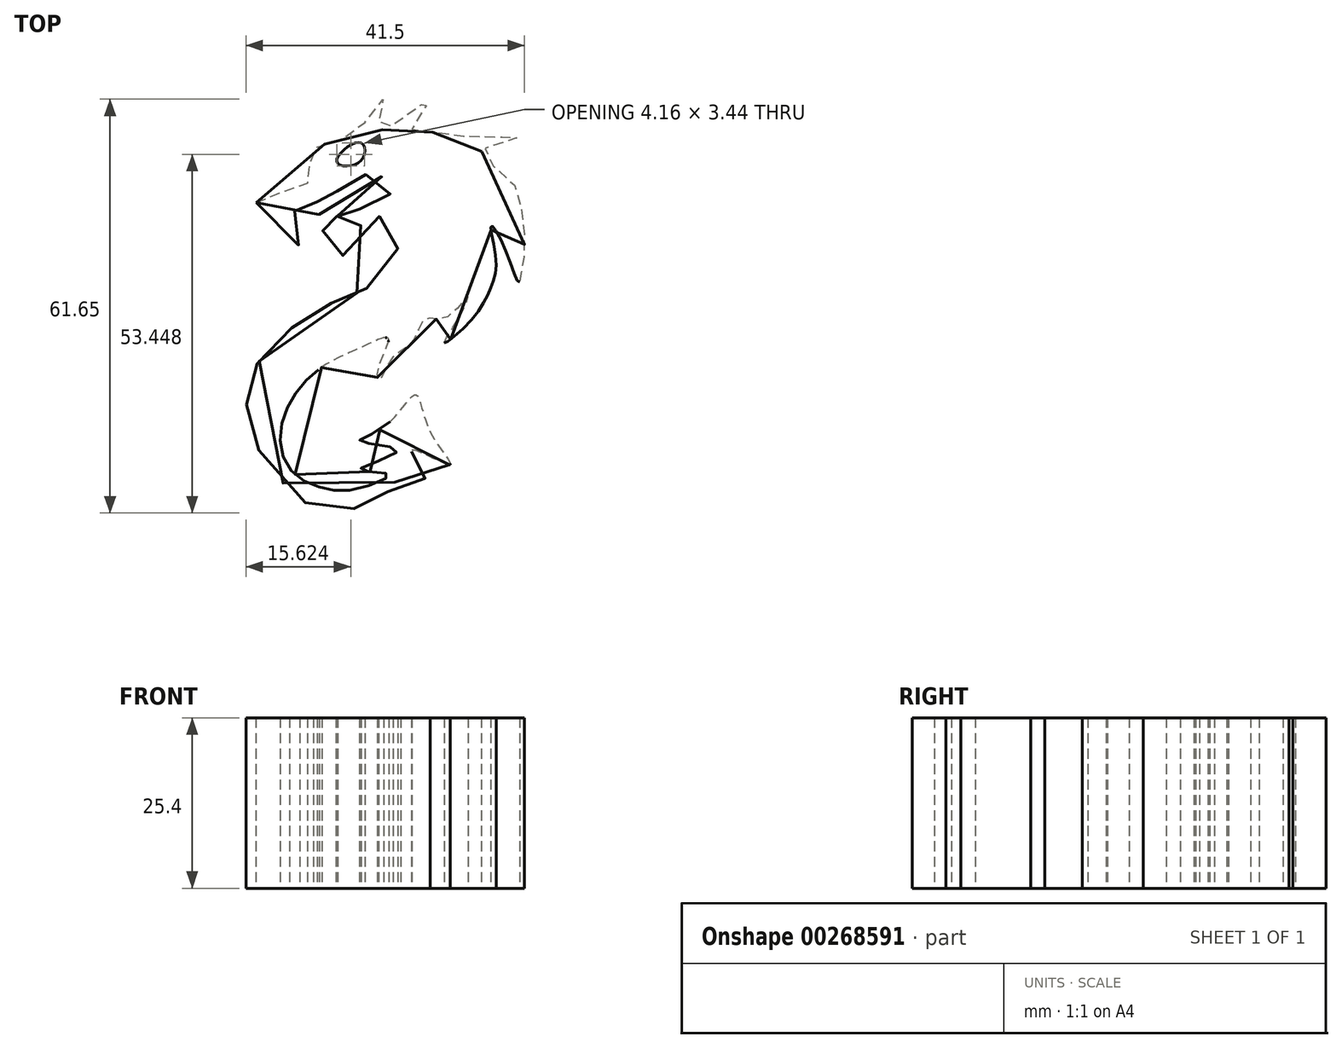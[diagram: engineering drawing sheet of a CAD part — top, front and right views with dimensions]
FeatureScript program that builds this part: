
annotation { "Feature Type Name" : "Feature", "Feature Type Description" : "" }
export const myFeature = defineFeature(function(context is Context, id is Id, definition is map)
    precondition{}
    {
        {
            var Q0;
            Q0=qCreatedBy(makeId("Top.planeOp"),FACE);
            var sketch = newSketch(context, id + "F0", { "sketchPlane" : qUnion([Q0])});
            skFitSpline(sketch, "E0", {"points": [v(-15.49, 17.26) * mm, v(-11.85, 18.65) * mm, v(-6.97, 21.44) * mm, v(-7.81, 24.23) * mm, v(-4.18, 26.32) * mm, v(0, 28.41) * mm, v(3.49, 32.6) * mm, v(2.79, 28.41) * mm, v(6.28, 29.8) * mm, v(10.46, 32.6) * mm, v(7.67, 28.41) * mm, v(11.16, 27.72) * mm, v(17.43, 27.02) * mm, v(23.7, 27.02) * mm, v(18.13, 24.93) * mm, v(21.61, 21.44) * mm, v(23.7, 17.95) * mm, v(24.4, 13.07) * mm, v(24.4, 9.59) * mm, v(23.7, 5.4) * mm, v(21.61, 10.28) * mm, v(19.52, 13.77) * mm, v(20.22, 8.9) * mm, v(19.52, 4.7) * mm, v(16.73, 0) * mm, v(12.55, -3.66) * mm, v(14.64, 0) * mm, v(16.04, 3.31) * mm, v(12.55, 0) * mm, v(9.76, 0) * mm, v(7.67, -3.66) * mm, v(4.88, -5.75) * mm, v(2.79, -9.24) * mm, v(2.79, -7.15) * mm, v(4.18, -2.96) * mm, v(0, -4.36) * mm, v(-5.58, -7.15) * mm, v(-9.76, -11.33) * mm, v(-11.85, -16.9) * mm, v(-10.46, -22.49) * mm, v(-5.58, -25.28) * mm, v(0, -25.28) * mm, v(4.18, -23.18) * mm, v(0, -22.49) * mm, v(5.58, -19.7) * mm, v(0, -18.3) * mm, v(3.49, -16.21) * mm, v(8.23, -11.33) * mm, v(10.46, -16.9) * mm, v(13.25, -21.79) * mm, v(7.67, -19.7) * mm, v(10.46, -23.88) * mm, v(6.97, -23.18) * mm, v(3.49, -26.67) * mm, v(0, -28.06) * mm, v(-5.58, -28.76) * mm, v(-14.64, -20.4) * mm, v(-16.73, -14.12) * mm, v(-16.73, -9.24) * mm, v(-13.25, -4.36) * mm, v(-8.37, 0) * mm, v(-3.49, 2.61) * mm, v(0, 4) * mm, v(4.18, 7.5) * mm, v(5.58, 14.47) * mm, v(0, 13.77) * mm, v(-3.49, 8.9) * mm, v(-5.58, 13.07) * mm, v(-3.49, 13.07) * mm, v(-3.49, 15.17) * mm, v(0, 15.17) * mm, v(0, 16.56) * mm, v(2.79, 17.26) * mm, v(4.88, 20.05) * mm, v(0, 21.44) * mm, v(-3.49, 20.05) * mm, v(-3.49, 17.95) * mm, v(-6.28, 17.95) * mm, v(-6.28, 15.17) * mm, v(-10.46, 15.86) * mm, v(-9.06, 10.98) * mm, v(-15.49, 17.26) * mm]});
            skSolve(sketch);
        }
        {
            var Q0;
            Q0=qCreatedBy(makeId("Top.planeOp"),FACE);
            var sketch = newSketch(context, id + "F1", { "sketchPlane" : qUnion([Q0])});
            skFitSpline(sketch, "E1", {"points": [v(-3.49, 23.4) * mm, v(0, 26.19) * mm, v(0, 23.4) * mm, v(-3.49, 23.4) * mm]});
            skSolve(sketch);
        }
        {
            var Q0;
            Q0=makeQuery(id+"F0.imprint","IMPRINT",FACE,{"disambiguationData":[TD([[makeQuery(id+"F0.imprint","IMPRINT",EDGE,{"derivedFrom":sQuery(id+"F0.wireOp",EDGE,"E0")}),-1.0]])]});
            extrude(context, id + "F2", {"entities" : qUnion([Q0]), "depth" : 25.4 * mm});
        }
        {
            var Q0;
            Q0=makeQuery(id+"F1.imprint","IMPRINT",FACE,{"disambiguationData":[TD([[makeQuery(id+"F1.imprint","IMPRINT",EDGE,{"derivedFrom":sQuery(id+"F1.wireOp",EDGE,"E1")}),-1.0]])]});
            extrude(context, id + "F3", {"entities" : qUnion([Q0]), "operationType" : NewBodyOperationType.REMOVE, "depth" : 25.4 * mm});
        }
    });
